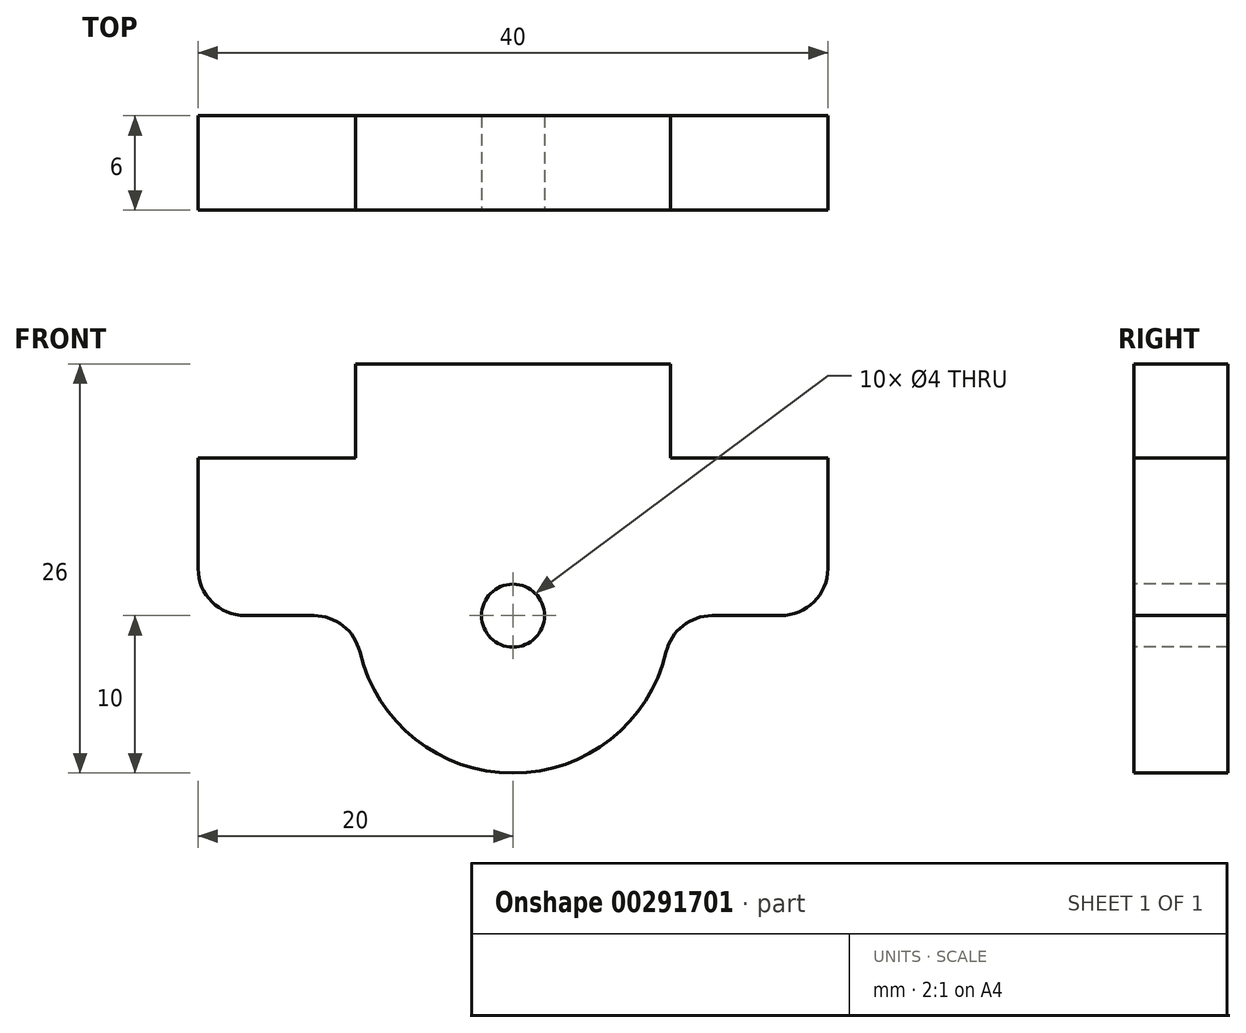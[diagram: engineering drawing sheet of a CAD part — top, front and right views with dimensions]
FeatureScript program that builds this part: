
annotation { "Feature Type Name" : "Feature", "Feature Type Description" : "" }
export const myFeature = defineFeature(function(context is Context, id is Id, definition is map)
    precondition{}
    {
        {
            var Q0;
            Q0=qCreatedBy(makeId("Front.planeOp"),FACE);
            var sketch = newSketch(context, id + "F0", { "sketchPlane" : qUnion([Q0])});
            skLineSegment(sketch, "E0", {"start": v(0, 0) * mm, "end": v(10, 0) * mm});
            skLineSegment(sketch, "E1", {"start": v(10, 0) * mm, "end": v(10, -6) * mm});
            skLineSegment(sketch, "E2", {"start": v(10, -6) * mm, "end": v(20, -6) * mm});
            skLineSegment(sketch, "E3", {"start": v(20, -6) * mm, "end": v(20, -16) * mm});
            skLineSegment(sketch, "E4", {"start": v(0, 0) * mm, "end": v(0, -26) * mm, "construction": true});
            skLineSegment(sketch, "E5.MirrorCS", {"start": v(-10, -6) * mm, "end": v(-20, -6) * mm});
            skLineSegment(sketch, "E6.MirrorCS", {"start": v(-20, -6) * mm, "end": v(-20, -16) * mm});
            skLineSegment(sketch, "E7.MirrorCS", {"start": v(0, 0) * mm, "end": v(-10, 0) * mm});
            skLineSegment(sketch, "E8.MirrorCS", {"start": v(-10, 0) * mm, "end": v(-10, -6) * mm});
            skLineSegment(sketch, "E9", {"start": v(20, -16) * mm, "end": v(10, -16) * mm});
            skArc(sketch, "E10", {"start": v(10, -16) * mm, "mid": v(7.07, -23.07) * mm, "end": v(0, -26) * mm});
            skLineSegment(sketch, "E11.MirrorCS", {"start": v(-20, -16) * mm, "end": v(-10, -16) * mm});
            skArc(sketch, "E12.MirrorCS", {"start": v(-10, -16) * mm, "mid": v(-7.07, -23.07) * mm, "end": v(0, -26) * mm});
            skSolve(sketch);
        }
        {
            var Q0;
            Q0=qSketchRegion(id+"F0",true);
            extrude(context, id + "F1", {"entities" : qUnion([Q0]), "depth" : 6 * mm});
        }
        {
            var Q0;
            Q0=makeQuery(id+"F1.opExtrude","CAP_FACE",FACE,{"disambiguationData":[OSD([sQuery(id+"F0.wireOp",EDGE,"E0"),sQuery(id+"F0.wireOp",EDGE,"E1"),sQuery(id+"F0.wireOp",EDGE,"E2"),sQuery(id+"F0.wireOp",EDGE,"E3"),sQuery(id+"F0.wireOp",EDGE,"E5.MirrorCS"),sQuery(id+"F0.wireOp",EDGE,"E6.MirrorCS"),sQuery(id+"F0.wireOp",EDGE,"E7.MirrorCS"),sQuery(id+"F0.wireOp",EDGE,"E8.MirrorCS"),sQuery(id+"F0.wireOp",EDGE,"E9"),sQuery(id+"F0.wireOp",EDGE,"E10"),sQuery(id+"F0.wireOp",EDGE,"E11.MirrorCS"),sQuery(id+"F0.wireOp",EDGE,"E12.MirrorCS")])],"isStart":false});
            var sketch = newSketch(context, id + "F2", { "sketchPlane" : qUnion([Q0])});
            skLineSegment(sketch, "E13", {"start": v(-10, -16) * mm, "end": v(10, -16) * mm, "construction": true});
            skCircle(sketch, "E14", {"center": v(0, -16) * mm, "radius": 2 * mm});
            skSolve(sketch);
        }
        {
            var Q0;
            Q0=makeQuery(id+"F1.opExtrude","SWEPT_EDGE",EDGE,{"disambiguationData":[OSD([sQuery(id+"F0.wireOp",EDGE,"E9"),sQuery(id+"F0.wireOp",EDGE,"E10")])]});
            var Q1;
            Q1=makeQuery(id+"F1.opExtrude","SWEPT_EDGE",EDGE,{"disambiguationData":[OSD([sQuery(id+"F0.wireOp",EDGE,"E11.MirrorCS"),sQuery(id+"F0.wireOp",EDGE,"E12.MirrorCS")])]});
            var Q2;
            Q2=makeQuery(id+"F1.opExtrude","SWEPT_EDGE",EDGE,{"disambiguationData":[OSD([sQuery(id+"F0.wireOp",EDGE,"E3"),sQuery(id+"F0.wireOp",EDGE,"E9")])]});
            var Q3;
            Q3=makeQuery(id+"F1.opExtrude","SWEPT_EDGE",EDGE,{"disambiguationData":[OSD([sQuery(id+"F0.wireOp",EDGE,"E6.MirrorCS"),sQuery(id+"F0.wireOp",EDGE,"E11.MirrorCS")])]});
            fillet(context, id + "F3", {"entities" : qUnion([Q0, Q1, Q2, Q3]), "radius" : 3 * mm, "tangentPropagation" : true, "allowEdgeOverflow" : false});
        }
        {
            var Q0;
            Q0=qSketchRegion(id+"F2",true);
            extrude(context, id + "F4", {"entities" : qUnion([Q0]), "operationType" : NewBodyOperationType.REMOVE, "endBound" : BoundingType.THROUGH_ALL, "oppositeDirection" : true, "depth" : 25 * mm});
        }
    });
